# Revit family: QF_Vollrath_6958301
name_source: partatom
category: Specialty Equipment
revit_build: Autodesk Revit 2016 (Build: 20151007_0715(x64)
units: mm (PartAtom-declared; Revit-internal decimal feet)

## family parameters
Always vertical = Yes
Cut with Voids When Loaded = No
OmniClass Number = 23.40.40.00
OmniClass Title = Food Service Equipment and Furnishings
Part Type = Normal
Room Calculation Point = No
Round Connector Dimension = Use Diameter
Shared = No
Work Plane-Based = Yes

## types (2) — shared parameters
Conn Plug = NEMA 6-20P
Cycle = 60 Hz
Default Elevation = 0.00"
Depth = 20.13"
Description = Induction Wok
Elec Conn Connection Height = 2.00"
FL Amps = 15 A
Foodservice Equipment Identifier = Yes
Manufacturer = Vollrath
Model = 6958301
Phase = 1
Weight in Pounds = 34
Width = 17.00"

## per-type parameters (varying)
| type | Apparent Power | Volts | Watts |
| 208/60/1 | 3037 VA | 208 V | 3000 W |
| 240/60/1 | 3504 VA | 240 V | 3500 W |

## geometry (parser evidence)
native form markers: Blend x39, Sweep x2
no freeform markers — native parametric forms only
